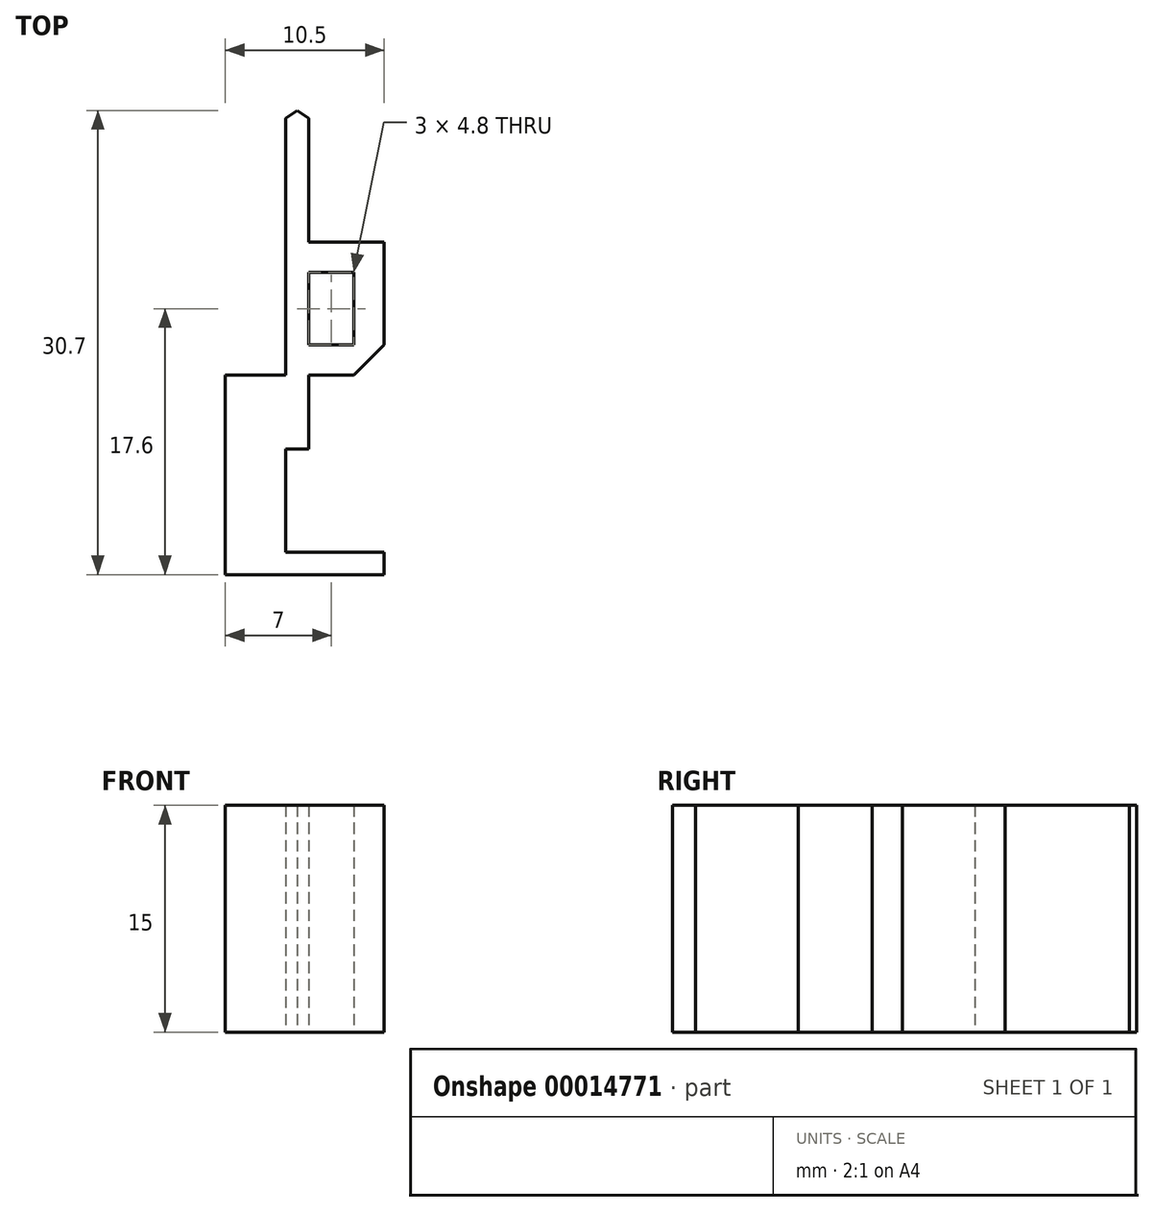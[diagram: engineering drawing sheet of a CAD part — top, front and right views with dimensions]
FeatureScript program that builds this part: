
annotation { "Feature Type Name" : "Feature", "Feature Type Description" : "" }
export const myFeature = defineFeature(function(context is Context, id is Id, definition is map)
    precondition{}
    {
        {
            var Q0;
            Q0=qCreatedBy(makeId("Top.planeOp"),FACE);
            var sketch = newSketch(context, id + "F0", { "sketchPlane" : qUnion([Q0])});
            skLineSegment(sketch, "E0", {"start": v(0, 17.4) * mm, "end": v(-0.75, 16.9) * mm});
            skLineSegment(sketch, "E1", {"start": v(-0.75, 16.9) * mm, "end": v(-0.75, -0.1) * mm});
            skLineSegment(sketch, "E2", {"start": v(-4.75, -1) * mm, "end": v(-4.75, -13.3) * mm});
            skLineSegment(sketch, "E3", {"start": v(-4.75, -13.3) * mm, "end": v(5.75, -13.3) * mm});
            skLineSegment(sketch, "E4", {"start": v(5.75, -13.3) * mm, "end": v(5.75, -11.8) * mm});
            skLineSegment(sketch, "E5", {"start": v(5.75, -11.8) * mm, "end": v(-0.75, -11.8) * mm});
            skLineSegment(sketch, "E6", {"start": v(-0.75, -11.8) * mm, "end": v(-0.75, -5) * mm});
            skLineSegment(sketch, "E7", {"start": v(-0.75, -5) * mm, "end": v(0.75, -5) * mm});
            skLineSegment(sketch, "E8", {"start": v(0.75, -5) * mm, "end": v(0.75, 0) * mm});
            skLineSegment(sketch, "E9", {"start": v(5.75, 1.9) * mm, "end": v(5.75, 8.7) * mm});
            skLineSegment(sketch, "E10", {"start": v(5.75, 8.7) * mm, "end": v(0.75, 8.7) * mm});
            skLineSegment(sketch, "E11", {"start": v(0.75, 8.7) * mm, "end": v(0.75, 16.9) * mm});
            skLineSegment(sketch, "E12", {"start": v(0.75, 16.9) * mm, "end": v(0, 17.4) * mm});
            skLineSegment(sketch, "E13", {"start": v(0.75, 6.7) * mm, "end": v(3.75, 6.7) * mm});
            skLineSegment(sketch, "E14", {"start": v(3.75, 6.7) * mm, "end": v(3.75, 1.9) * mm});
            skLineSegment(sketch, "E15", {"start": v(3.75, 1.9) * mm, "end": v(0.75, 1.9) * mm});
            skLineSegment(sketch, "E16", {"start": v(0.75, 1.9) * mm, "end": v(0.75, 6.7) * mm});
            skLineSegment(sketch, "E17", {"start": v(-1.25, -3) * mm, "end": v(-2.75, -3) * mm});
            skLineSegment(sketch, "E18", {"start": v(-2.75, -3) * mm, "end": v(-2.75, -3) * mm});
            skLineSegment(sketch, "E19", {"start": v(-2.75, -11.8) * mm, "end": v(-2.75, -11.8) * mm});
            skLineSegment(sketch, "E20", {"start": v(-2.75, -3) * mm, "end": v(-1.25, -3) * mm});
            skLineSegment(sketch, "E21", {"start": v(-1.25, -3) * mm, "end": v(-1.25, -3) * mm});
            skLineSegment(sketch, "E22", {"start": v(3.75, -0.1) * mm, "end": v(0.75, -0.1) * mm});
            skLineSegment(sketch, "E23", {"start": v(0.75, 0) * mm, "end": v(0.75, -0.1) * mm});
            skPoint(sketch, "E24.orphan", {"position": v(5.75, 0) * mm});
            skLineSegment(sketch, "E25", {"start": v(5.75, 1.9) * mm, "end": v(3.75, -0.1) * mm});
            skPoint(sketch, "E26.orphan", {"position": v(5.75, -0.1) * mm});
            skLineSegment(sketch, "E27", {"start": v(-0.75, -0.1) * mm, "end": v(-4.75, -0.1) * mm});
            skLineSegment(sketch, "E28", {"start": v(-4.75, -0.1) * mm, "end": v(-4.75, -1) * mm});
            skPoint(sketch, "E29.start.orphan", {"position": v(-0.75, 0) * mm});
            skSolve(sketch);
        }
        {
            var Q0;
            Q0=makeQuery(id+"F0.imprint","IMPRINT",FACE,{"disambiguationData":[TD([[makeQuery(id+"F0.imprint","IMPRINT",EDGE,{"derivedFrom":sQuery(id+"F0.wireOp",EDGE,"E0")}),1.0]])]});
            extrude(context, id + "F1", {"entities" : qUnion([Q0]), "depth" : 15 * mm});
        }
    });
